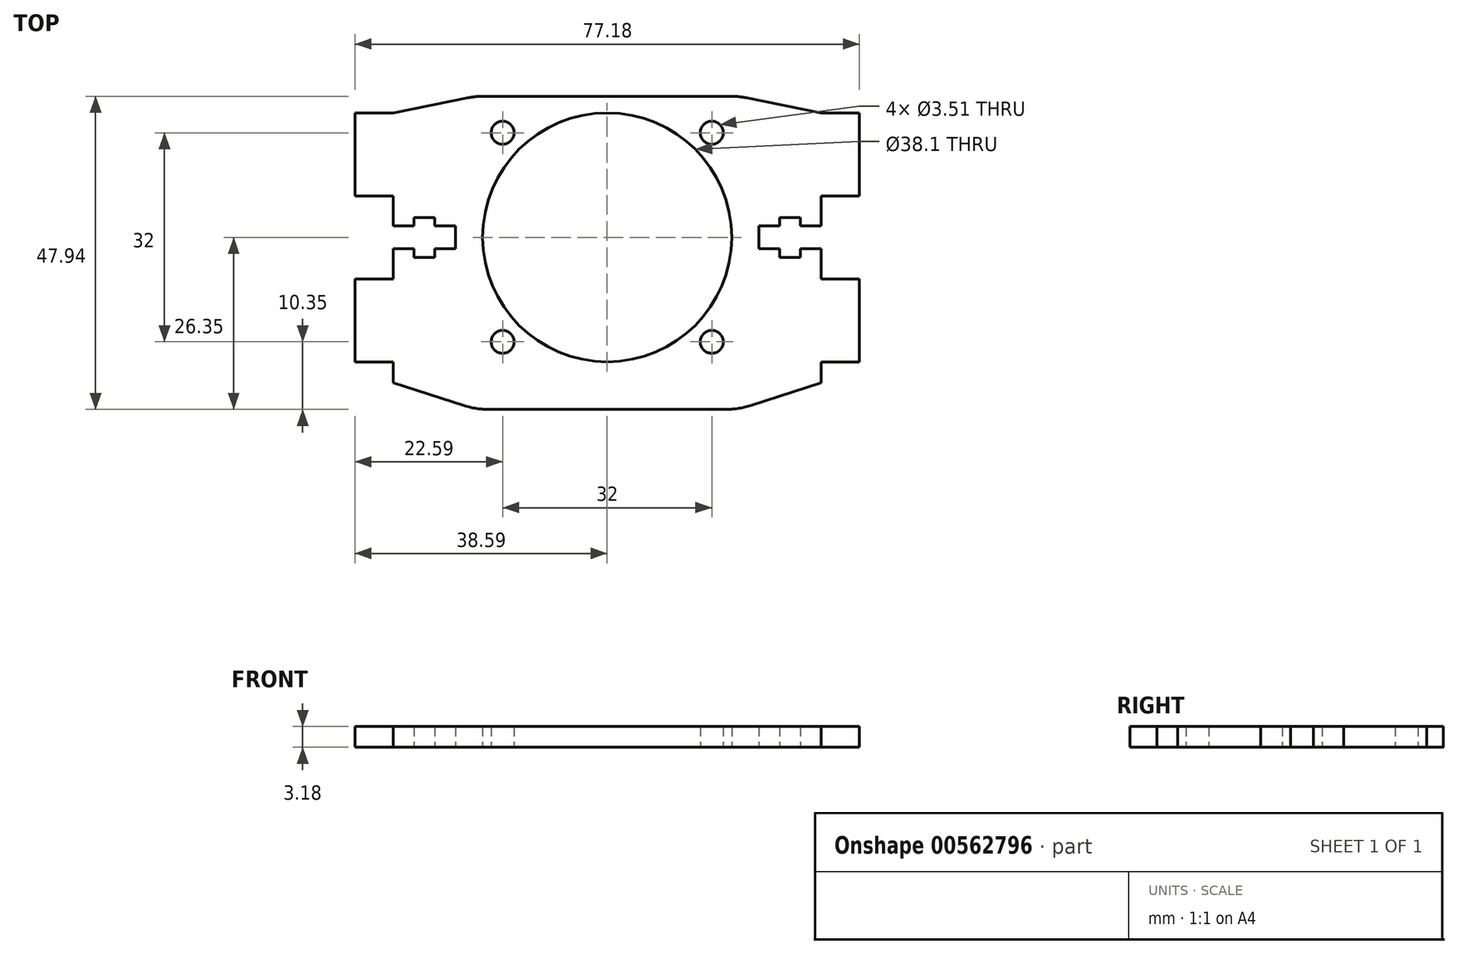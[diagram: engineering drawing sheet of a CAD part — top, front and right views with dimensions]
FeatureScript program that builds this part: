
annotation { "Feature Type Name" : "Feature", "Feature Type Description" : "" }
export const myFeature = defineFeature(function(context is Context, id is Id, definition is map)
    precondition{}
    {
        {
            var Q0;
            Q0=qCreatedBy(makeId("Top.planeOp"),FACE);
            var sketch = newSketch(context, id + "F0", { "sketchPlane" : qUnion([Q0])});
            skCircle(sketch, "E0", {"center": v(0, 0) * mm, "radius": 19.05 * mm});
            skCircle(sketch, "E1", {"center": v(16, 16) * mm, "radius": 1.75 * mm});
            skLineSegment(sketch, "E2.right", {"start": v(20, 20) * mm, "end": v(20, -20) * mm});
            skCircle(sketch, "E3.MirrorC", {"center": v(-16, 16) * mm, "radius": 1.75 * mm});
            skCircle(sketch, "E4.MirrorC", {"center": v(16, -16) * mm, "radius": 1.75 * mm});
            skCircle(sketch, "E5.MirrorC", {"center": v(-16, -16) * mm, "radius": 1.75 * mm});
            skLineSegment(sketch, "E6.bottom", {"start": v(-32.75, -6.35) * mm, "end": v(-38.6, -6.35) * mm});
            skLineSegment(sketch, "E6.top", {"start": v(-32.75, -19.05) * mm, "end": v(-38.6, -19.05) * mm});
            skLineSegment(sketch, "E6.right", {"start": v(-38.6, -6.35) * mm, "end": v(-38.6, -19.05) * mm});
            skPoint(sketch, "E6.middle", {"position": v(-35.67, -12.7) * mm});
            skLineSegment(sketch, "E7", {"start": v(-20, -26.35) * mm, "end": v(0, -26.35) * mm});
            skLineSegment(sketch, "E8.bottom", {"start": v(-38.6, 6.35) * mm, "end": v(-32.75, 6.35) * mm});
            skLineSegment(sketch, "E8.top", {"start": v(-38.6, 19.05) * mm, "end": v(-32.75, 19.05) * mm});
            skLineSegment(sketch, "E8.left", {"start": v(-38.6, 6.35) * mm, "end": v(-38.6, 19.05) * mm});
            skPoint(sketch, "E8.middle", {"position": v(-35.67, 12.7) * mm});
            skLineSegment(sketch, "E9", {"start": v(-32.75, 6.35) * mm, "end": v(-32.75, 1.75) * mm});
            skLineSegment(sketch, "E10", {"start": v(-32.75, 19.05) * mm, "end": v(-20, 21.59) * mm});
            skLineSegment(sketch, "E11", {"start": v(-20, 21.59) * mm, "end": v(0, 21.59) * mm});
            skPoint(sketch, "E2.left.start.orphan", {"position": v(-20, 20) * mm});
            skPoint(sketch, "E2.top.start.orphan", {"position": v(-20, -20) * mm});
            skLineSegment(sketch, "E12.MirrorCS", {"start": v(20, 21.59) * mm, "end": v(0, 21.59) * mm});
            skLineSegment(sketch, "E13.MirrorCS", {"start": v(32.75, 19.05) * mm, "end": v(20, 21.59) * mm});
            skLineSegment(sketch, "E14.MirrorCS", {"start": v(38.6, 19.05) * mm, "end": v(32.75, 19.05) * mm});
            skLineSegment(sketch, "E15.MirrorCS", {"start": v(38.6, 6.35) * mm, "end": v(38.6, 19.05) * mm});
            skLineSegment(sketch, "E16.MirrorCS", {"start": v(38.6, 6.35) * mm, "end": v(32.75, 6.35) * mm});
            skLineSegment(sketch, "E17.MirrorCS", {"start": v(32.75, 6.35) * mm, "end": v(32.75, 1.75) * mm});
            skLineSegment(sketch, "E18.MirrorCS", {"start": v(32.75, -6.35) * mm, "end": v(38.6, -6.35) * mm});
            skLineSegment(sketch, "E19.MirrorCS", {"start": v(38.6, -6.35) * mm, "end": v(38.6, -19.05) * mm});
            skLineSegment(sketch, "E20.MirrorCS", {"start": v(32.75, -19.05) * mm, "end": v(38.6, -19.05) * mm});
            skLineSegment(sketch, "E21.MirrorCS", {"start": v(20, -26.35) * mm, "end": v(0, -26.35) * mm});
            skLineSegment(sketch, "E22.bottom", {"start": v(-32.75, 1.75) * mm, "end": v(-29.57, 1.75) * mm});
            skLineSegment(sketch, "E22.top", {"start": v(-32.75, -1.75) * mm, "end": v(-29.57, -1.75) * mm});
            skPoint(sketch, "E22.middle", {"position": v(-31.16, 0) * mm});
            skLineSegment(sketch, "E23.bottom", {"start": v(-29.57, 3.05) * mm, "end": v(-26.4, 3.05) * mm});
            skLineSegment(sketch, "E23.top", {"start": v(-29.57, -3.05) * mm, "end": v(-26.4, -3.05) * mm});
            skLineSegment(sketch, "E23.left", {"start": v(-29.57, 3.05) * mm, "end": v(-29.57, 1.75) * mm});
            skLineSegment(sketch, "E23.right", {"start": v(-26.4, 3.05) * mm, "end": v(-26.4, 1.75) * mm});
            skPoint(sketch, "E23.middle", {"position": v(-27.99, 0) * mm});
            skLineSegment(sketch, "E24.bottom", {"start": v(-26.4, 1.75) * mm, "end": v(-23.22, 1.75) * mm});
            skLineSegment(sketch, "E24.top", {"start": v(-26.4, -1.75) * mm, "end": v(-23.22, -1.75) * mm});
            skLineSegment(sketch, "E24.right", {"start": v(-23.22, 1.75) * mm, "end": v(-23.22, -1.75) * mm});
            skPoint(sketch, "E24.middle", {"position": v(-24.81, 0) * mm});
            skLineSegment(sketch, "E25.trimOffspring", {"start": v(-29.57, -1.75) * mm, "end": v(-29.57, -3.05) * mm});
            skLineSegment(sketch, "E26.trimOffspring", {"start": v(-32.75, -1.75) * mm, "end": v(-32.75, -6.35) * mm});
            skLineSegment(sketch, "E27.trimOffspring", {"start": v(-26.4, -1.75) * mm, "end": v(-26.4, -3.05) * mm});
            skLineSegment(sketch, "E28.MirrorCS", {"start": v(29.57, -1.75) * mm, "end": v(29.57, -3.05) * mm});
            skLineSegment(sketch, "E29.MirrorCS", {"start": v(29.57, 3.05) * mm, "end": v(29.57, 1.75) * mm});
            skLineSegment(sketch, "E30.MirrorCS", {"start": v(26.4, 3.05) * mm, "end": v(26.4, 1.75) * mm});
            skLineSegment(sketch, "E31.MirrorCS", {"start": v(26.4, -1.75) * mm, "end": v(26.4, -3.05) * mm});
            skLineSegment(sketch, "E32.MirrorCS", {"start": v(29.57, -3.05) * mm, "end": v(26.4, -3.05) * mm});
            skLineSegment(sketch, "E33.MirrorCS", {"start": v(26.4, 1.75) * mm, "end": v(23.22, 1.75) * mm});
            skLineSegment(sketch, "E34.MirrorCS", {"start": v(29.57, 3.05) * mm, "end": v(26.4, 3.05) * mm});
            skLineSegment(sketch, "E35.MirrorCS", {"start": v(32.75, 1.75) * mm, "end": v(29.57, 1.75) * mm});
            skLineSegment(sketch, "E36.MirrorCS", {"start": v(26.4, -1.75) * mm, "end": v(23.22, -1.75) * mm});
            skLineSegment(sketch, "E37.MirrorCS", {"start": v(32.75, -1.75) * mm, "end": v(32.75, -6.35) * mm});
            skPoint(sketch, "E38.MirrorP", {"position": v(27.99, 0) * mm});
            skPoint(sketch, "E39.MirrorP", {"position": v(24.81, 0) * mm});
            skPoint(sketch, "E40.MirrorP", {"position": v(31.16, 0) * mm});
            skLineSegment(sketch, "E41.MirrorCS", {"start": v(32.75, -1.75) * mm, "end": v(29.57, -1.75) * mm});
            skLineSegment(sketch, "E42.MirrorCS", {"start": v(23.22, 1.75) * mm, "end": v(23.22, -1.75) * mm});
            skLineSegment(sketch, "E43", {"start": v(-32.75, -19.05) * mm, "end": v(-32.75, -22.23) * mm});
            skLineSegment(sketch, "E44", {"start": v(-32.75, -22.23) * mm, "end": v(-20, -26.35) * mm});
            skPoint(sketch, "E45.MirrorCS.end.orphan", {"position": v(20, -26.35) * mm});
            skPoint(sketch, "E45.MirrorCS.start.orphan", {"position": v(32.75, -19.05) * mm});
            skLineSegment(sketch, "E46.MirrorCS", {"start": v(32.75, -19.05) * mm, "end": v(32.75, -22.23) * mm});
            skLineSegment(sketch, "E47.MirrorCS", {"start": v(32.75, -22.23) * mm, "end": v(20, -26.35) * mm});
            skSolve(sketch);
        }
        {
            var Q0;
            Q0 = qSketchRegion(id + "F0", true);
            extrude(context, id + "F1", {"entities" : qUnion([Q0]), "depth" : 3.17 * mm, "offsetDistance" : 25.4 * mm});
        }
        {
            var Q0;
            Q0=makeQuery(id+"F1.opExtrude","SWEPT_EDGE",EDGE,{"disambiguationData":[OSD([sQuery(id+"F0.wireOp",EDGE,"E7"),sQuery(id+"F0.wireOp",EDGE,"E44")])]});
            var Q1;
            Q1=makeQuery(id+"F1.opExtrude","SWEPT_EDGE",EDGE,{"disambiguationData":[OSD([sQuery(id+"F0.wireOp",EDGE,"E21.MirrorCS"),sQuery(id+"F0.wireOp",EDGE,"E47.MirrorCS")])]});
            var Q2;
            Q2=makeQuery(id+"F1.opExtrude","SWEPT_EDGE",EDGE,{"disambiguationData":[OSD([sQuery(id+"F0.wireOp",EDGE,"E12.MirrorCS"),sQuery(id+"F0.wireOp",EDGE,"E13.MirrorCS")])]});
            var Q3;
            Q3=makeQuery(id+"F1.opExtrude","SWEPT_EDGE",EDGE,{"disambiguationData":[OSD([sQuery(id+"F0.wireOp",EDGE,"E10"),sQuery(id+"F0.wireOp",EDGE,"E11")])]});
            fillet(context, id + "F2", {"entities" : qUnion([Q0, Q1, Q2, Q3]), "radius" : 12.7 * mm, "tangentPropagation" : true, "allowEdgeOverflow" : false});
        }
    });
